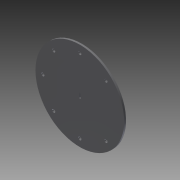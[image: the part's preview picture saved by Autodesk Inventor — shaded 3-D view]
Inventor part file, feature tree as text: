
AUTODESK INVENTOR PART (.ipt)
format: ipt  version: 2015 (Build 190159000, 159)  size: 179,200 bytes
history: native  units: mm
features: extrude x4, sketch x4, projected_geometry x3
ambient origin geometry x8: Origin, YZ Plane, XZ Plane, XY Plane, X Axis, Y Axis, Z Axis, Center Point
bodies: Solid1 (feature_tree)
feature tree (11):
  extrude  "Extrusion1"  Depth=2.5mm TaperAngle=0.0deg
  extrude  "Extrusion2"  Depth=20.0mm
  extrude  "Extrusion3"  Depth=18.0mm TaperAngle=0.0deg
  extrude  "Extrusion4"  Depth=2.0mm
  sketch  "Sketch1"  dims[d0=120.0mm d1=2.5mm d2=0.0mm]
  sketch  "Sketch2"  dims[d3=20.0mm d4=15.0mm]
  sketch  "Sketch4"  dims[d5=8.0mm d6=18.0mm d7=0.0mm]
  projected_geometry  "Projected Loop2"
  projected_geometry  "Projected Loop3"
  sketch  "Sketch5"  dims[d8=8.0mm d9=25.0mm d10=20.0mm d11=0.0mm d13=120.0mm d15=20.0mm d16=0.0mm d17=6.0mm d18=2.0mm d19=50.0mm d20=0.0mm d21=50.0mm d22=45.0deg d23=50.0mm d24=90.0deg d25=50.0mm d26=135.0deg d27=50.0mm d28=180.0deg d29=50.0mm d30=135.0deg d31=50.0mm d32=90.0deg d33=50.0mm d34=45.0deg d35=4.2mm d36=4.2mm d37=4.2mm d38=4.2mm d39=4.2mm d40=4.2mm d41=4.2mm d42=4.2mm]
  projected_geometry  "Projected Loop4"
